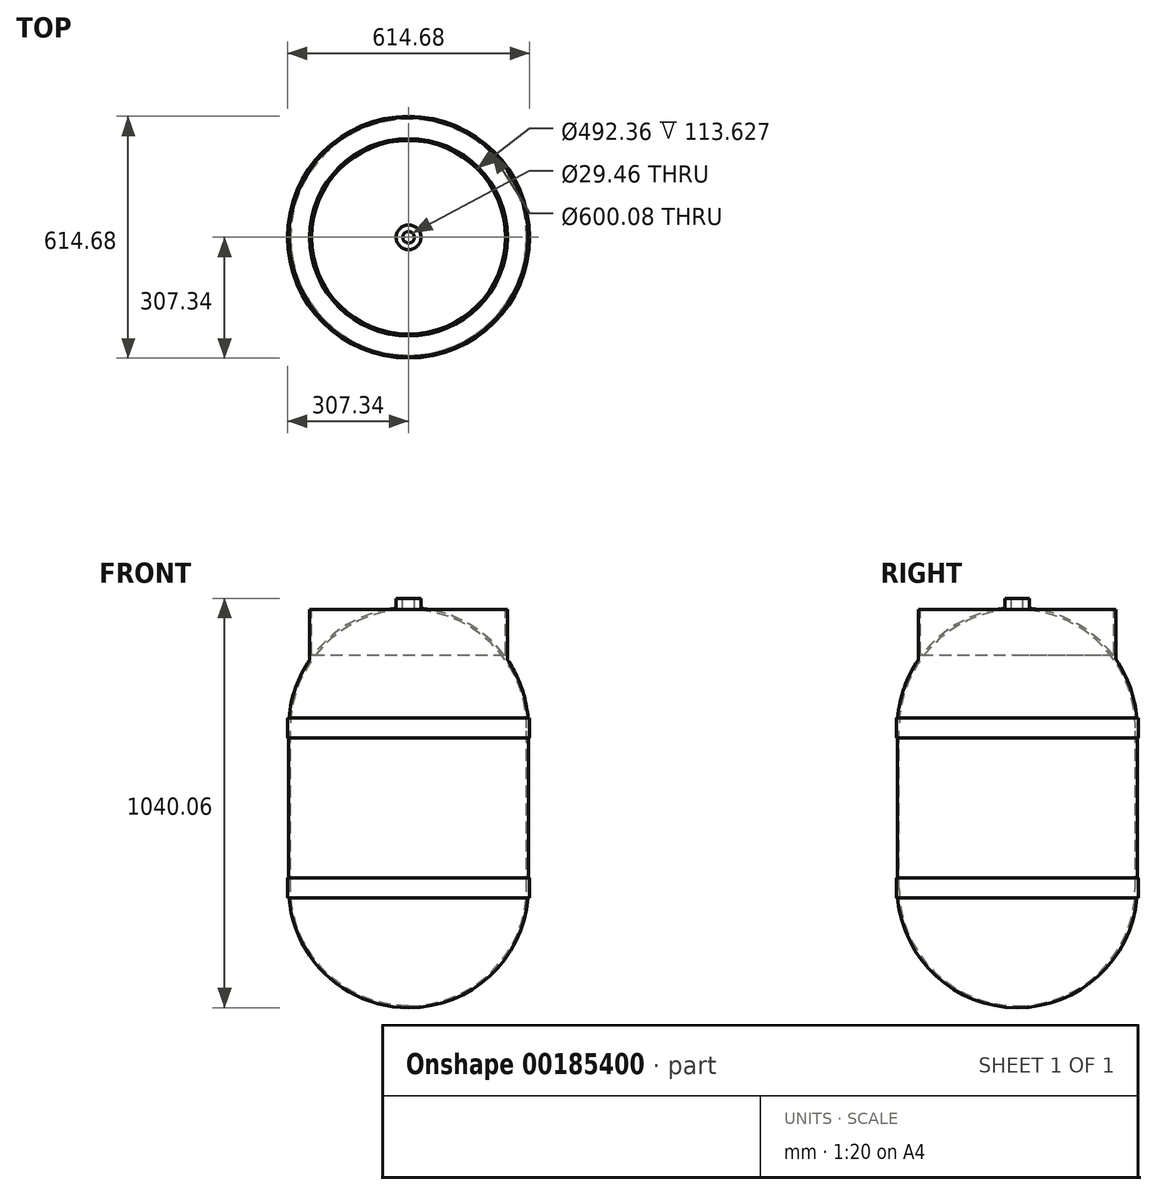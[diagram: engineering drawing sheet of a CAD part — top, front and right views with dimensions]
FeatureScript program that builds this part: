
annotation { "Feature Type Name" : "Feature", "Feature Type Description" : "" }
export const myFeature = defineFeature(function(context is Context, id is Id, definition is map)
    precondition{}
    {
        {
            var Q0;
            Q0=qCreatedBy(makeId("Front.planeOp"),FACE);
            var sketch = newSketch(context, id + "F0", { "sketchPlane" : qUnion([Q0])});
            skLineSegment(sketch, "E0", {"start": v(0, 0) * mm, "end": v(0, 508) * mm});
            skLineSegment(sketch, "E1", {"start": v(0, 508) * mm, "end": v(-304.8, 508) * mm});
            skLineSegment(sketch, "E2", {"start": v(0, 0) * mm, "end": v(0, -508) * mm});
            skLineSegment(sketch, "E3", {"start": v(0, 508) * mm, "end": v(0, 203.2) * mm});
            skLineSegment(sketch, "E4", {"start": v(-304.8, 508) * mm, "end": v(-304.8, 203.2) * mm});
            skArc(sketch, "E5", {"start": v(0, 508) * mm, "mid": v(-215.53, 418.73) * mm, "end": v(-304.8, 203.2) * mm});
            skLineSegment(sketch, "E6", {"start": v(0, 0) * mm, "end": v(-304.8, 0) * mm});
            skLineSegment(sketch, "E7", {"start": v(-304.8, 203.2) * mm, "end": v(-304.8, 0) * mm});
            skArc(sketch, "E8.MirrorCS", {"start": v(0, 508) * mm, "mid": v(134.67, 476.63) * mm, "end": v(241.63, 389) * mm});
            skArc(sketch, "E9.MirrorCS", {"start": v(251.39, 375.56) * mm, "mid": v(291.14, 293.42) * mm, "end": v(304.8, 203.2) * mm});
            skLineSegment(sketch, "E10.MirrorCS", {"start": v(304.8, 203.2) * mm, "end": v(304.8, 0) * mm});
            skArc(sketch, "E11.MirrorCS", {"start": v(0, -508) * mm, "mid": v(-215.53, -418.73) * mm, "end": v(-304.8, -203.2) * mm});
            skLineSegment(sketch, "E12.MirrorCS", {"start": v(-304.8, -203.2) * mm, "end": v(-304.8, 0) * mm});
            skArc(sketch, "E13.MirrorCS", {"start": v(0, -508) * mm, "mid": v(215.53, -418.73) * mm, "end": v(304.8, -203.2) * mm});
            skLineSegment(sketch, "E14.MirrorCS", {"start": v(304.8, -203.2) * mm, "end": v(304.8, 0) * mm});
            skLineSegment(sketch, "E15", {"start": v(304.8, 203.2) * mm, "end": v(307.34, 203.2) * mm});
            skLineSegment(sketch, "E16", {"start": v(307.34, 203.2) * mm, "end": v(307.34, 177.8) * mm});
            skLineSegment(sketch, "E17", {"start": v(307.34, 203.2) * mm, "end": v(307.34, 228.6) * mm});
            skLineSegment(sketch, "E18", {"start": v(307.34, 177.8) * mm, "end": v(304.8, 177.8) * mm});
            skLineSegment(sketch, "E19", {"start": v(307.34, 228.6) * mm, "end": v(303.74, 228.6) * mm});
            skArc(sketch, "E20.0", {"start": v(0, -503.24) * mm, "mid": v(212.16, -415.36) * mm, "end": v(300.04, -203.2) * mm});
            skLineSegment(sketch, "E20.1", {"start": v(300.04, -203.2) * mm, "end": v(300.04, 0) * mm});
            skLineSegment(sketch, "E20.2", {"start": v(300.04, 203.2) * mm, "end": v(300.04, 0) * mm});
            skArc(sketch, "E20.3", {"start": v(0, 503.24) * mm, "mid": v(212.16, 415.36) * mm, "end": v(300.04, 203.2) * mm});
            skLineSegment(sketch, "E21", {"start": v(28.58, 508) * mm, "end": v(28.58, 506.66) * mm});
            skLineSegment(sketch, "E22", {"start": v(31.4, 509.23) * mm, "end": v(31.4, 532.06) * mm});
            skLineSegment(sketch, "E23", {"start": v(31.4, 532.06) * mm, "end": v(0, 532.06) * mm});
            skLineSegment(sketch, "E24", {"start": v(0, 532.06) * mm, "end": v(0, 508) * mm});
            skPoint(sketch, "E25.newPointA", {"position": v(0, 508) * mm});
            skPoint(sketch, "E25.newPointB", {"position": v(31.4, 506.66) * mm});
            skArc(sketch, "E25.filletArc", {"start": v(31.4, 509.23) * mm, "mid": v(32.2, 507.11) * mm, "end": v(34.21, 506.07) * mm});
            skLineSegment(sketch, "E26", {"start": v(304.8, -203.2) * mm, "end": v(307.34, -203.2) * mm});
            skLineSegment(sketch, "E27", {"start": v(307.34, -203.2) * mm, "end": v(307.34, -228.6) * mm});
            skLineSegment(sketch, "E28", {"start": v(307.34, -203.2) * mm, "end": v(307.34, -177.8) * mm});
            skLineSegment(sketch, "E29", {"start": v(307.34, -177.8) * mm, "end": v(304.8, -177.8) * mm});
            skLineSegment(sketch, "E30", {"start": v(307.34, -228.6) * mm, "end": v(303.74, -228.6) * mm});
            skLineSegment(sketch, "E31", {"start": v(0, 377.17) * mm, "end": v(250.28, 377.17) * mm});
            skLineSegment(sketch, "E32", {"start": v(250.94, 377) * mm, "end": v(250.94, 504.17) * mm});
            skLineSegment(sketch, "E33", {"start": v(250.94, 504.17) * mm, "end": v(246.18, 504.17) * mm});
            skLineSegment(sketch, "E34", {"start": v(246.18, 504.17) * mm, "end": v(246.18, 390.54) * mm});
            skPoint(sketch, "E35.newPointA", {"position": v(304.8, 203.2) * mm});
            skArc(sketch, "E35.filletArc", {"start": v(241.63, 389) * mm, "mid": v(244.46, 388.14) * mm, "end": v(246.18, 390.54) * mm});
            skPoint(sketch, "E36.newPointA", {"position": v(250.94, 377.17) * mm});
            skArc(sketch, "E36.filletArc", {"start": v(250.94, 377) * mm, "mid": v(251.06, 376.24) * mm, "end": v(251.39, 375.56) * mm});
            skSolve(sketch);
        }
        {
            var Q0;
            Q0=makeQuery(id+"F0.imprint","IMPRINT",FACE,{"disambiguationData":[TD([[makeQuery(id+"F0.imprint","IMPRINT",EDGE,{"derivedFrom":sQuery(id+"F0.wireOp",EDGE,"E22")}),1.0]])]});
            var Q1;
            {var subQ5=sQuery(id+"F0.wireOp",EDGE,"E13.MirrorCS");Q1=makeQuery(id+"F0.imprint","IMPRINT",FACE,{"disambiguationData":[TD([[makeQuery(id+"F0.imprint","IMPRINT",EDGE,{"derivedFrom":subQ5}),1.0]])]});}
            var Q2;
            {var subQ0=sQuery(id+"F0.wireOp",EDGE,"E15");Q2=makeQuery(id+"F0.imprint","IMPRINT",FACE,{"disambiguationData":[TD([[makeQuery(id+"F0.imprint","IMPRINT",EDGE,{"derivedFrom":subQ0}),-1.0]])]});}
            var Q3;
            {var subQ0=sQuery(id+"F0.wireOp",EDGE,"E15");Q3=makeQuery(id+"F0.imprint","IMPRINT",FACE,{"disambiguationData":[TD([[makeQuery(id+"F0.imprint","IMPRINT",EDGE,{"derivedFrom":subQ0}),1.0]])]});}
            var Q4;
            {var subQ0=sQuery(id+"F0.wireOp",EDGE,"E26");Q4=makeQuery(id+"F0.imprint","IMPRINT",FACE,{"disambiguationData":[TD([[makeQuery(id+"F0.imprint","IMPRINT",EDGE,{"derivedFrom":subQ0}),-1.0]])]});}
            var Q5;
            {var subQ0=sQuery(id+"F0.wireOp",EDGE,"E26");Q5=makeQuery(id+"F0.imprint","IMPRINT",FACE,{"disambiguationData":[TD([[makeQuery(id+"F0.imprint","IMPRINT",EDGE,{"derivedFrom":subQ0}),1.0]])]});}
            var Q6;
            Q6=sQuery(id+"F0.wireOp",EDGE,"E3");
            revolve(context, id + "F1", {"entities" : qUnion([Q0, Q1, Q2, Q3, Q4, Q5]), "axis" : qUnion([Q6]), "revolveType" : RevolveType.FULL});
        }
        {
            var Q0;
            Q0=makeQuery(id+"F1.opRevolve","SWEPT_FACE",FACE,{"disambiguationData":[OSD([sQuery(id+"F0.wireOp",EDGE,"E23")])]});
            var sketch = newSketch(context, id + "F2", { "sketchPlane" : qUnion([Q0])});
            skCircle(sketch, "E37", {"center": v(0, 0) * mm, "radius": 14.73 * mm});
            skSolve(sketch);
        }
        {
            var Q0;
            Q0=makeQuery(id+"F2.imprint","IMPRINT",FACE,{"disambiguationData":[TD([[makeQuery(id+"F2.imprint","IMPRINT",EDGE,{"derivedFrom":sQuery(id+"F2.wireOp",EDGE,"E37")}),1.0]])]});
            extrude(context, id + "F3", {"entities" : qUnion([Q0]), "operationType" : NewBodyOperationType.REMOVE, "oppositeDirection" : true, "depth" : 76.2 * mm});
        }
    });
